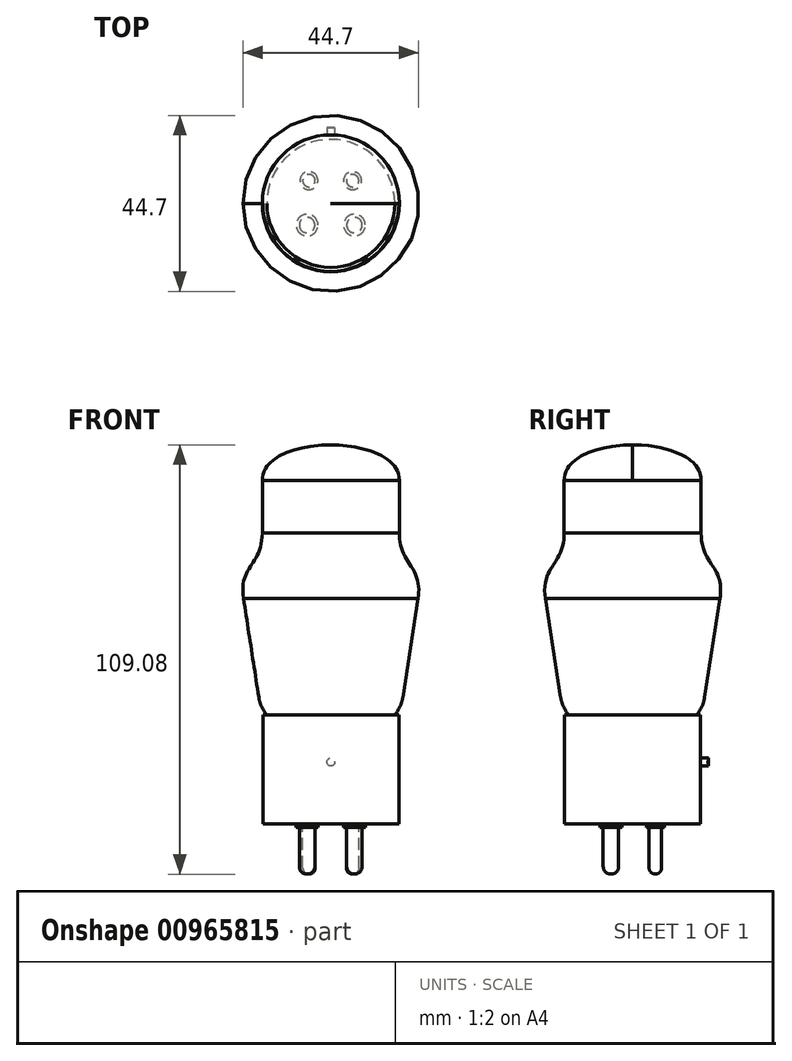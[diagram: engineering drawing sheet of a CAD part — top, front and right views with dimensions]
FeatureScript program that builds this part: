
annotation { "Feature Type Name" : "Feature", "Feature Type Description" : "" }
export const myFeature = defineFeature(function(context is Context, id is Id, definition is map)
    precondition{}
    {
        {
            var Q0;
            Q0=qCreatedBy(makeId("Front.planeOp"),FACE);
            var sketch = newSketch(context, id + "F0", { "sketchPlane" : qUnion([Q0])});
            skLineSegment(sketch, "E0", {"start": v(0, 0) * mm, "end": v(17.27, 0) * mm});
            skLineSegment(sketch, "E1", {"start": v(17.27, 0) * mm, "end": v(17.27, 27.76) * mm});
            skLineSegment(sketch, "E2", {"start": v(17.27, 27.76) * mm, "end": v(16.26, 27.76) * mm});
            skLineSegment(sketch, "E3", {"start": v(16.26, 27.76) * mm, "end": v(16.26, 17.4) * mm, "construction": true});
            skLineSegment(sketch, "E4", {"start": v(18.29, 32.2) * mm, "end": v(22.17, 57.3) * mm});
            skLineSegment(sketch, "E5", {"start": v(17.4, 73.96) * mm, "end": v(17.4, 87.32) * mm});
            skLineSegment(sketch, "E6", {"start": v(0, 96.34) * mm, "end": v(-6.17, 96.34) * mm, "construction": true});
            skFitSpline(sketch, "E7", {"points": [v(0, 96.34) * mm, v(17.4, 87.32) * mm], "startDerivative": vector(22.95, 0) * mm, "endDerivative": vector(0, -19.12) * mm});
            skLineSegment(sketch, "E8", {"start": v(22.17, 57.3) * mm, "end": v(-22.17, 57.3) * mm, "construction": true});
            skLineSegment(sketch, "E9", {"start": v(18.29, 32.2) * mm, "end": v(-18.29, 32.2) * mm, "construction": true});
            skFitSpline(sketch, "E10", {"points": [v(17.4, 73.96) * mm, v(22.17, 57.3) * mm], "startDerivative": vector(0, -24.52) * mm, "endDerivative": vector(-3.84, -24.81) * mm});
            skArc(sketch, "E11", {"start": v(18.29, 32.2) * mm, "mid": v(17.58, 29.84) * mm, "end": v(16.26, 27.76) * mm});
            skLineSegment(sketch, "E12", {"start": v(0, 0) * mm, "end": v(-17.27, 0) * mm, "construction": true});
            skPoint(sketch, "E13", {"position": v(0, 32.2) * mm});
            skPoint(sketch, "E14", {"position": v(0, 57.3) * mm});
            skLineSegment(sketch, "E15", {"start": v(17.4, 73.96) * mm, "end": v(0, 73.96) * mm, "construction": true});
            skLineSegment(sketch, "E16", {"start": v(0, 73.96) * mm, "end": v(-17.4, 73.96) * mm, "construction": true});
            skPoint(sketch, "E17", {"position": v(22.35, 59.47) * mm});
            skLineSegment(sketch, "E18", {"start": v(22.35, 59.47) * mm, "end": v(-22.35, 59.47) * mm, "construction": true});
            skLineSegment(sketch, "E19", {"start": v(22.35, 59.47) * mm, "end": v(22.35, 70.88) * mm, "construction": true});
            skPoint(sketch, "E20", {"position": v(0, 59.47) * mm});
            skLineSegment(sketch, "E21", {"start": v(0, 0) * mm, "end": v(0, 96.34) * mm});
            skSolve(sketch);
        }
        {
            var Q0;
            Q0=makeQuery(id+"F0.imprint","IMPRINT",FACE,{"disambiguationData":[TD([[makeQuery(id+"F0.imprint","IMPRINT",EDGE,{"derivedFrom":sQuery(id+"F0.wireOp",EDGE,"E0")}),1.0]])]});
            var Q1;
            Q1=sQuery(id+"F0.wireOp",EDGE,"E21");
            revolve(context, id + "F1", {"surfaceOperationType" : NewSurfaceOperationType.NEW, "entities" : qUnion([Q0]), "axis" : qUnion([Q1]), "revolveType" : RevolveType.FULL});
        }
        {
            var Q0;
            Q0=makeQuery(id+"F1.opRevolve","SWEPT_FACE",FACE,{"disambiguationData":[OSD([sQuery(id+"F0.wireOp",EDGE,"E0")])]});
            var sketch = newSketch(context, id + "F2", { "sketchPlane" : qUnion([Q0])});
            skCircle(sketch, "E22", {"center": v(-6.01, 5.52) * mm, "radius": 2.77 * mm});
            skCircle(sketch, "E23", {"center": v(-5.54, -5.76) * mm, "radius": 2.29 * mm});
            skLineSegment(sketch, "E24", {"start": v(0, 0) * mm, "end": v(0, -17.27) * mm, "construction": true});
            skLineSegment(sketch, "E25", {"start": v(-5.54, -8.05) * mm, "end": v(0, -8.05) * mm, "construction": true});
            skLineSegment(sketch, "E26", {"start": v(0, -8.05) * mm, "end": v(5.54, -8.05) * mm, "construction": true});
            skLineSegment(sketch, "E27", {"start": v(-6.01, 2.76) * mm, "end": v(0, 2.76) * mm, "construction": true});
            skLineSegment(sketch, "E28", {"start": v(0, 2.76) * mm, "end": v(6.01, 2.76) * mm, "construction": true});
            skLineSegment(sketch, "E29", {"start": v(-5.54, -3.48) * mm, "end": v(-6.01, 2.76) * mm, "construction": true});
            skCircle(sketch, "E30.MirrorC", {"center": v(6.01, 5.52) * mm, "radius": 2.77 * mm});
            skCircle(sketch, "E31.MirrorC", {"center": v(5.54, -5.76) * mm, "radius": 2.29 * mm});
            skLineSegment(sketch, "E32", {"start": v(-8, 7.46) * mm, "end": v(7.18, -7.36) * mm, "construction": true});
            skLineSegment(sketch, "E33", {"start": v(-3.26, -5.76) * mm, "end": v(3.26, -5.76) * mm, "construction": true});
            skLineSegment(sketch, "E34", {"start": v(-3.24, 5.52) * mm, "end": v(3.24, 5.52) * mm, "construction": true});
            skLineSegment(sketch, "E35", {"start": v(-6.01, -17.27) * mm, "end": v(-6.01, 8.3) * mm, "construction": true});
            skSolve(sketch);
        }
        {
            var Q0;
            Q0 = qSketchRegion(id + "F2", true);
            extrude(context, id + "F3", {"entities" : qUnion([Q0]), "operationType" : NewBodyOperationType.ADD, "depth" : 0.85 * mm, "offsetDistance" : 25.4 * mm});
        }
        {
            var Q0;
            Q0=makeQuery(id+"F3.opExtrude","CAP_FACE",FACE,{"disambiguationData":[OSD([sQuery(id+"F2.wireOp",EDGE,"E22")])],"isStart":false});
            var sketch = newSketch(context, id + "F4", { "sketchPlane" : qUnion([Q0])});
            skCircle(sketch, "E36", {"center": v(-5.54, -5.76) * mm, "radius": 1.58 * mm});
            skCircle(sketch, "E37", {"center": v(5.54, -5.76) * mm, "radius": 1.58 * mm});
            skCircle(sketch, "E38", {"center": v(-6.01, 5.52) * mm, "radius": 1.97 * mm});
            skCircle(sketch, "E39", {"center": v(6.01, 5.52) * mm, "radius": 1.97 * mm});
            skSolve(sketch);
        }
        {
            var Q0;
            Q0 = qSketchRegion(id + "F4", true);
            extrude(context, id + "F5", {"entities" : qUnion([Q0]), "operationType" : NewBodyOperationType.ADD, "depth" : 11.9 * mm, "offsetDistance" : 25.4 * mm});
        }
        {
            var Q0;
            Q0=makeQuery(id+"F5.opExtrude","CAP_EDGE",EDGE,{"disambiguationData":[OSD([sQuery(id+"F4.wireOp",EDGE,"E38")])],"isStart":false});
            var Q1;
            Q1=makeQuery(id+"F5.opExtrude","CAP_EDGE",EDGE,{"disambiguationData":[OSD([sQuery(id+"F4.wireOp",EDGE,"E39")])],"isStart":false});
            fillet(context, id + "F6", {"entities" : qUnion([Q0, Q1]), "radius" : 1.97 * mm, "tangentPropagation" : true, "allowEdgeOverflow" : false});
        }
        {
            var Q0;
            Q0=makeQuery(id+"F5.opExtrude","CAP_EDGE",EDGE,{"disambiguationData":[OSD([sQuery(id+"F4.wireOp",EDGE,"E36")])],"isStart":false});
            var Q1;
            Q1=makeQuery(id+"F5.opExtrude","CAP_EDGE",EDGE,{"disambiguationData":[OSD([sQuery(id+"F4.wireOp",EDGE,"E37")])],"isStart":false});
            fillet(context, id + "F7", {"entities" : qUnion([Q0, Q1]), "radius" : 1.57 * mm, "tangentPropagation" : true, "allowEdgeOverflow" : false});
        }
        {
            var Q0;
            Q0=qCreatedBy(makeId("Front.planeOp"),FACE);
            var sketch = newSketch(context, id + "F8", { "sketchPlane" : qUnion([Q0])});
            skCircle(sketch, "E40", {"center": v(0, 15.74) * mm, "radius": 1 * mm});
            skLineSegment(sketch, "E41", {"start": v(0, 14.73) * mm, "end": v(0, 0) * mm, "construction": true});
            skSolve(sketch);
        }
        {
            var Q0;
            Q0 = qSketchRegion(id + "F8", true);
            var Q1;
            Q1=makeQuery(id+"F1.opRevolve","SWEPT_FACE",FACE,{"disambiguationData":[OSD([sQuery(id+"F0.wireOp",EDGE,"E1")])]});
            extrude(context, id + "F9", {"entities" : qUnion([Q0]), "operationType" : NewBodyOperationType.ADD, "endBound" : BoundingType.UP_TO_SURFACE, "oppositeDirection" : true, "depth" : 25.4 * mm, "endBoundEntityFace" : qUnion([Q1]), "hasOffset" : true, "offsetDistance" : 1.94 * mm, "offsetOppositeDirection" : true});
        }
    });
